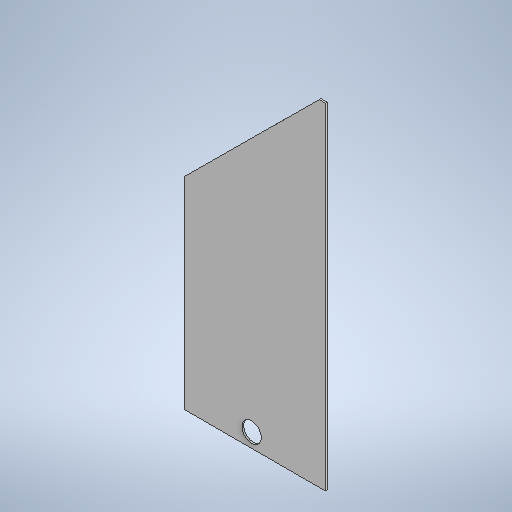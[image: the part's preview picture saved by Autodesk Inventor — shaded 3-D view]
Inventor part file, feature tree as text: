
AUTODESK INVENTOR PART (.ipt)
format: ipt  version: 2025 (Build 290162010, 162A)  size: 378,368 bytes
history: native  units: mm
features: extrude x3, sketch x2, fillet x1, pattern_circular x1, projected_geometry x1, other x1
ambient origin geometry x8: Origin, YZ Plane, XZ Plane, XY Plane, X Axis, Y Axis, Z Axis, Center Point
bodies: Solid1 (feature_tree)
feature tree (9):
  extrude  "Extrusion1"  Depth=1180.0mm
  fillet  "Fillet1"  Radius=1180.0mm
  extrude  "Extrusion4"  Depth=10.0mm
  pattern_circular  "Circular Pattern3"  Count=191  [1 undecoded]
  extrude  "Extrusion5"  [1 undecoded]
  sketch  "Sketch4"  dims[d1=840.0mm d3=1150.0mm d12=1180.0mm]
  sketch  "Sketch5"  dims[d13=950.0mm d14=111.0mm d15=1910.0mm d17=-521.637743mm d18=377.0mm d19=-269.216713mm d24=10.0mm d25=0.0mm d34=380.0mm d35=80.0mm d37=2140.0mm d52=530.0mm d53=5.0mm d54=10.0mm d55=30.0mm d56=10.0mm d59=265.0mm d60=13.0mm d61=1.963495mm d62=10.0mm d63=0.0mm d64=160.0mm d65=360.0deg d67=5.0mm d68=5.0mm d69=780.0mm d71=1078.0mm d72=340.0mm d73=1340.0mm d74=0.0mm d75=0.0mm d70=0.872665mm]
  projected_geometry  "Projected Loop1"
  other  "Definition1"
note: 2 required parameter values undecoded (feature->parameter linkage not recoverable at this tier; creation-order binding heuristic only, values carry confidence <= 0.55)
